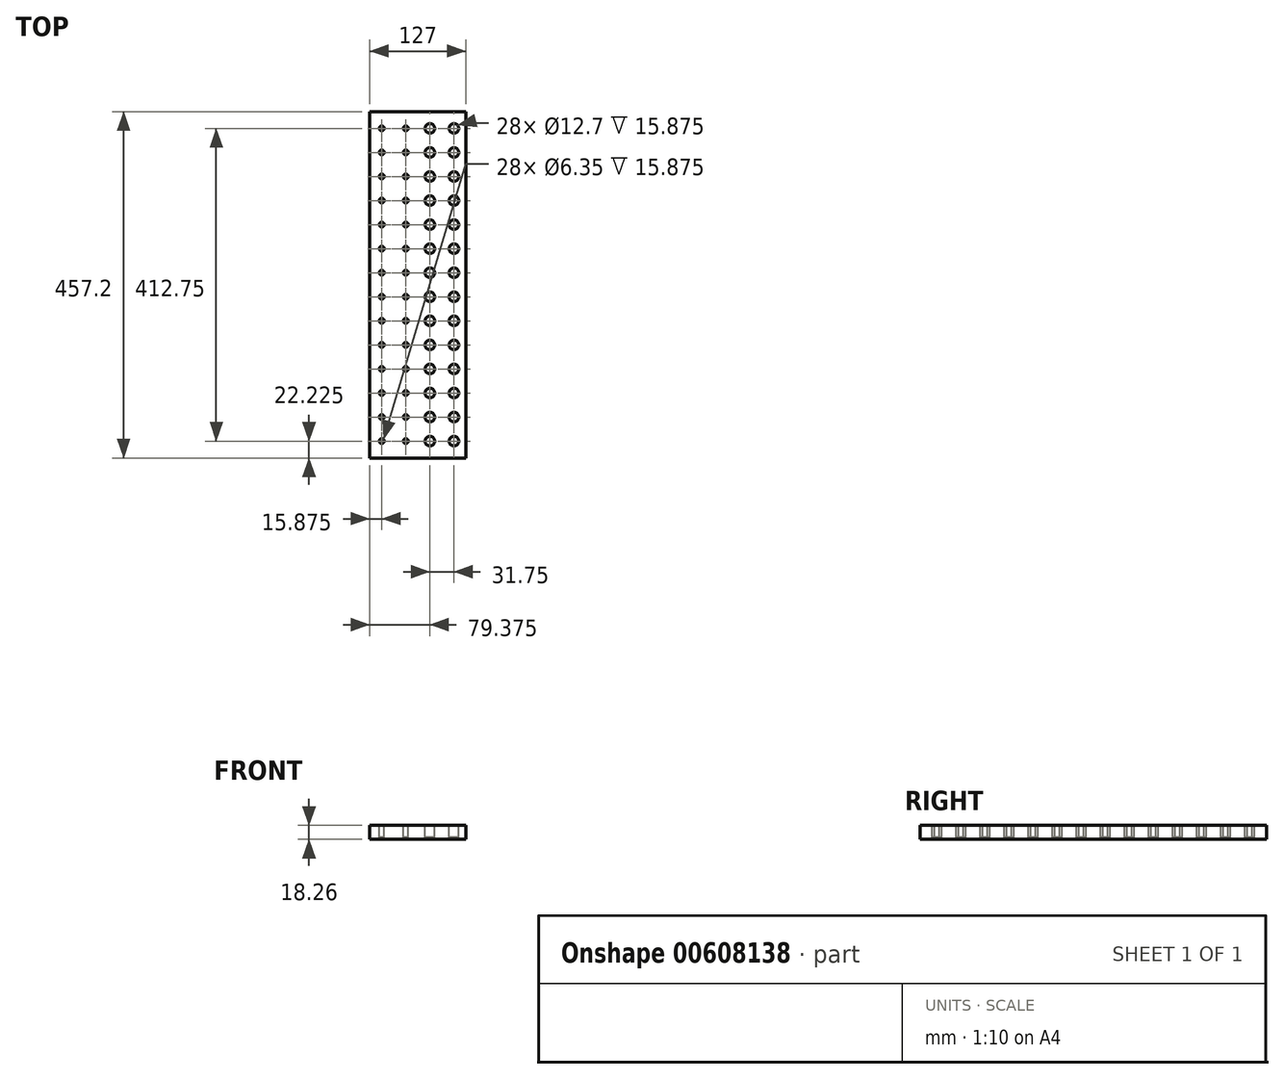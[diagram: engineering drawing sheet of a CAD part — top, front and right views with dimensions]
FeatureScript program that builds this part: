
annotation { "Feature Type Name" : "Feature", "Feature Type Description" : "" }
export const myFeature = defineFeature(function(context is Context, id is Id, definition is map)
    precondition{}
    {
        {
            var Q0;
            Q0=qCreatedBy(makeId("Top.planeOp"),FACE);
            var sketch = newSketch(context, id + "F0", { "sketchPlane" : qUnion([Q0])});
            skLineSegment(sketch, "E0.bottom", {"start": v(63.5, -228.6) * mm, "end": v(-63.5, -228.6) * mm});
            skLineSegment(sketch, "E0.top", {"start": v(63.5, 228.6) * mm, "end": v(-63.5, 228.6) * mm});
            skLineSegment(sketch, "E0.left", {"start": v(63.5, -228.6) * mm, "end": v(63.5, 228.6) * mm});
            skLineSegment(sketch, "E0.right", {"start": v(-63.5, -228.6) * mm, "end": v(-63.5, 228.6) * mm});
            skPoint(sketch, "E0.middle", {"position": v(0, 0) * mm});
            skSolve(sketch);
        }
        {
            var Q0;
            Q0 = qSketchRegion(id + "F0", true);
            extrude(context, id + "F1", {"entities" : qUnion([Q0]), "depth" : 18.26 * mm, "offsetDistance" : 25.4 * mm});
        }
        {
            var Q0;
            Q0=makeQuery(id+"F1.opExtrude","CAP_FACE",FACE,{"disambiguationData":[OSD([sQuery(id+"F0.wireOp",EDGE,"E0.bottom"),sQuery(id+"F0.wireOp",EDGE,"E0.top"),sQuery(id+"F0.wireOp",EDGE,"E0.left"),sQuery(id+"F0.wireOp",EDGE,"E0.right")])],"isStart":false});
            var sketch = newSketch(context, id + "F2", { "sketchPlane" : qUnion([Q0])});
            skCircle(sketch, "E1", {"center": v(-47.63, 206.38) * mm, "radius": 15.88 * mm, "construction": true});
            skCircle(sketch, "E2.0.1.0", {"center": v(-47.63, 174.63) * mm, "radius": 15.88 * mm, "construction": true});
            skCircle(sketch, "E2.0.2.0", {"center": v(-47.63, 142.88) * mm, "radius": 15.88 * mm, "construction": true});
            skCircle(sketch, "E2.0.3.0", {"center": v(-47.63, 111.13) * mm, "radius": 15.88 * mm, "construction": true});
            skCircle(sketch, "E2.0.4.0", {"center": v(-47.63, 79.38) * mm, "radius": 15.88 * mm, "construction": true});
            skCircle(sketch, "E2.0.5.0", {"center": v(-47.63, 47.63) * mm, "radius": 15.88 * mm, "construction": true});
            skCircle(sketch, "E2.0.6.0", {"center": v(-47.63, 15.88) * mm, "radius": 15.88 * mm, "construction": true});
            skCircle(sketch, "E2.0.7.0", {"center": v(-47.63, -15.87) * mm, "radius": 15.88 * mm, "construction": true});
            skCircle(sketch, "E2.0.8.0", {"center": v(-47.63, -47.62) * mm, "radius": 15.88 * mm, "construction": true});
            skCircle(sketch, "E2.0.9.0", {"center": v(-47.63, -79.37) * mm, "radius": 15.88 * mm, "construction": true});
            skCircle(sketch, "E2.0.10.0", {"center": v(-47.63, -111.12) * mm, "radius": 15.88 * mm, "construction": true});
            skCircle(sketch, "E2.0.11.0", {"center": v(-47.63, -142.87) * mm, "radius": 15.88 * mm, "construction": true});
            skCircle(sketch, "E2.0.12.0", {"center": v(-47.63, -174.62) * mm, "radius": 15.88 * mm, "construction": true});
            skCircle(sketch, "E2.0.13.0", {"center": v(-47.63, -206.37) * mm, "radius": 15.88 * mm, "construction": true});
            skCircle(sketch, "E2.1.0.0", {"center": v(-15.88, 206.38) * mm, "radius": 15.88 * mm, "construction": true});
            skCircle(sketch, "E2.1.1.0", {"center": v(-15.88, 174.63) * mm, "radius": 15.88 * mm, "construction": true});
            skCircle(sketch, "E2.1.2.0", {"center": v(-15.88, 142.88) * mm, "radius": 15.88 * mm, "construction": true});
            skCircle(sketch, "E2.1.3.0", {"center": v(-15.88, 111.13) * mm, "radius": 15.88 * mm, "construction": true});
            skCircle(sketch, "E2.1.4.0", {"center": v(-15.88, 79.38) * mm, "radius": 15.88 * mm, "construction": true});
            skCircle(sketch, "E2.1.5.0", {"center": v(-15.88, 47.63) * mm, "radius": 15.88 * mm, "construction": true});
            skCircle(sketch, "E2.1.6.0", {"center": v(-15.88, 15.88) * mm, "radius": 15.88 * mm, "construction": true});
            skCircle(sketch, "E2.1.7.0", {"center": v(-15.88, -15.87) * mm, "radius": 15.88 * mm, "construction": true});
            skCircle(sketch, "E2.1.8.0", {"center": v(-15.88, -47.62) * mm, "radius": 15.88 * mm, "construction": true});
            skCircle(sketch, "E2.1.9.0", {"center": v(-15.88, -79.37) * mm, "radius": 15.88 * mm, "construction": true});
            skCircle(sketch, "E2.1.10.0", {"center": v(-15.88, -111.12) * mm, "radius": 15.88 * mm, "construction": true});
            skCircle(sketch, "E2.1.11.0", {"center": v(-15.88, -142.87) * mm, "radius": 15.88 * mm, "construction": true});
            skCircle(sketch, "E2.1.12.0", {"center": v(-15.88, -174.62) * mm, "radius": 15.88 * mm, "construction": true});
            skCircle(sketch, "E2.1.13.0", {"center": v(-15.88, -206.37) * mm, "radius": 15.88 * mm, "construction": true});
            skCircle(sketch, "E2.2.0.0", {"center": v(15.87, 206.38) * mm, "radius": 15.88 * mm, "construction": true});
            skCircle(sketch, "E2.2.1.0", {"center": v(15.87, 174.63) * mm, "radius": 15.88 * mm, "construction": true});
            skCircle(sketch, "E2.2.2.0", {"center": v(15.87, 142.88) * mm, "radius": 15.88 * mm, "construction": true});
            skCircle(sketch, "E2.2.3.0", {"center": v(15.87, 111.13) * mm, "radius": 15.88 * mm, "construction": true});
            skCircle(sketch, "E2.2.4.0", {"center": v(15.87, 79.38) * mm, "radius": 15.88 * mm, "construction": true});
            skCircle(sketch, "E2.2.5.0", {"center": v(15.87, 47.63) * mm, "radius": 15.88 * mm, "construction": true});
            skCircle(sketch, "E2.2.6.0", {"center": v(15.87, 15.88) * mm, "radius": 15.88 * mm, "construction": true});
            skCircle(sketch, "E2.2.7.0", {"center": v(15.87, -15.87) * mm, "radius": 15.88 * mm, "construction": true});
            skCircle(sketch, "E2.2.8.0", {"center": v(15.87, -47.62) * mm, "radius": 15.88 * mm, "construction": true});
            skCircle(sketch, "E2.2.9.0", {"center": v(15.87, -79.37) * mm, "radius": 15.88 * mm, "construction": true});
            skCircle(sketch, "E2.2.10.0", {"center": v(15.87, -111.12) * mm, "radius": 15.88 * mm, "construction": true});
            skCircle(sketch, "E2.2.11.0", {"center": v(15.87, -142.87) * mm, "radius": 15.88 * mm, "construction": true});
            skCircle(sketch, "E2.2.12.0", {"center": v(15.87, -174.62) * mm, "radius": 15.88 * mm, "construction": true});
            skCircle(sketch, "E2.2.13.0", {"center": v(15.87, -206.37) * mm, "radius": 15.88 * mm, "construction": true});
            skCircle(sketch, "E2.3.0.0", {"center": v(47.62, 206.38) * mm, "radius": 15.88 * mm, "construction": true});
            skCircle(sketch, "E2.3.1.0", {"center": v(47.62, 174.63) * mm, "radius": 15.88 * mm, "construction": true});
            skCircle(sketch, "E2.3.2.0", {"center": v(47.62, 142.88) * mm, "radius": 15.88 * mm, "construction": true});
            skCircle(sketch, "E2.3.3.0", {"center": v(47.62, 111.13) * mm, "radius": 15.88 * mm, "construction": true});
            skCircle(sketch, "E2.3.4.0", {"center": v(47.62, 79.38) * mm, "radius": 15.88 * mm, "construction": true});
            skCircle(sketch, "E2.3.5.0", {"center": v(47.62, 47.63) * mm, "radius": 15.88 * mm, "construction": true});
            skCircle(sketch, "E2.3.6.0", {"center": v(47.62, 15.88) * mm, "radius": 15.88 * mm, "construction": true});
            skCircle(sketch, "E2.3.7.0", {"center": v(47.62, -15.87) * mm, "radius": 15.88 * mm, "construction": true});
            skCircle(sketch, "E2.3.8.0", {"center": v(47.62, -47.62) * mm, "radius": 15.88 * mm, "construction": true});
            skCircle(sketch, "E2.3.9.0", {"center": v(47.62, -79.37) * mm, "radius": 15.88 * mm, "construction": true});
            skCircle(sketch, "E2.3.10.0", {"center": v(47.62, -111.12) * mm, "radius": 15.88 * mm, "construction": true});
            skCircle(sketch, "E2.3.11.0", {"center": v(47.62, -142.87) * mm, "radius": 15.88 * mm, "construction": true});
            skCircle(sketch, "E2.3.12.0", {"center": v(47.62, -174.62) * mm, "radius": 15.88 * mm, "construction": true});
            skCircle(sketch, "E2.3.13.0", {"center": v(47.62, -206.37) * mm, "radius": 15.88 * mm, "construction": true});
            skLineSegment(sketch, "E2.direction1", {"start": v(-47.63, 206.38) * mm, "end": v(-15.88, 206.38) * mm, "construction": true});
            skLineSegment(sketch, "E2.direction2", {"start": v(-47.63, 206.38) * mm, "end": v(-47.63, 174.63) * mm, "construction": true});
            skCircle(sketch, "E3", {"center": v(47.62, 206.38) * mm, "radius": 6.35 * mm});
            skCircle(sketch, "E4", {"center": v(-47.63, 206.38) * mm, "radius": 3.18 * mm});
            skCircle(sketch, "E5.0.1.0", {"center": v(47.62, 174.63) * mm, "radius": 6.35 * mm});
            skCircle(sketch, "E5.0.2.0", {"center": v(47.62, 142.88) * mm, "radius": 6.35 * mm});
            skCircle(sketch, "E5.0.3.0", {"center": v(47.62, 111.13) * mm, "radius": 6.35 * mm});
            skCircle(sketch, "E5.0.4.0", {"center": v(47.62, 79.38) * mm, "radius": 6.35 * mm});
            skCircle(sketch, "E5.0.5.0", {"center": v(47.62, 47.63) * mm, "radius": 6.35 * mm});
            skCircle(sketch, "E5.0.6.0", {"center": v(47.62, 15.88) * mm, "radius": 6.35 * mm});
            skCircle(sketch, "E5.0.7.0", {"center": v(47.62, -15.87) * mm, "radius": 6.35 * mm});
            skCircle(sketch, "E5.0.8.0", {"center": v(47.62, -47.62) * mm, "radius": 6.35 * mm});
            skCircle(sketch, "E5.0.9.0", {"center": v(47.62, -79.37) * mm, "radius": 6.35 * mm});
            skCircle(sketch, "E5.0.10.0", {"center": v(47.62, -111.12) * mm, "radius": 6.35 * mm});
            skCircle(sketch, "E5.0.11.0", {"center": v(47.62, -142.87) * mm, "radius": 6.35 * mm});
            skCircle(sketch, "E5.0.12.0", {"center": v(47.62, -174.62) * mm, "radius": 6.35 * mm});
            skCircle(sketch, "E5.0.13.0", {"center": v(47.62, -206.37) * mm, "radius": 6.35 * mm});
            skCircle(sketch, "E5.1.0.0", {"center": v(15.87, 206.38) * mm, "radius": 6.35 * mm});
            skCircle(sketch, "E5.1.1.0", {"center": v(15.87, 174.63) * mm, "radius": 6.35 * mm});
            skCircle(sketch, "E5.1.2.0", {"center": v(15.87, 142.88) * mm, "radius": 6.35 * mm});
            skCircle(sketch, "E5.1.3.0", {"center": v(15.87, 111.13) * mm, "radius": 6.35 * mm});
            skCircle(sketch, "E5.1.4.0", {"center": v(15.87, 79.38) * mm, "radius": 6.35 * mm});
            skCircle(sketch, "E5.1.5.0", {"center": v(15.87, 47.63) * mm, "radius": 6.35 * mm});
            skCircle(sketch, "E5.1.6.0", {"center": v(15.87, 15.88) * mm, "radius": 6.35 * mm});
            skCircle(sketch, "E5.1.7.0", {"center": v(15.87, -15.87) * mm, "radius": 6.35 * mm});
            skCircle(sketch, "E5.1.8.0", {"center": v(15.87, -47.62) * mm, "radius": 6.35 * mm});
            skCircle(sketch, "E5.1.9.0", {"center": v(15.87, -79.37) * mm, "radius": 6.35 * mm});
            skCircle(sketch, "E5.1.10.0", {"center": v(15.87, -111.12) * mm, "radius": 6.35 * mm});
            skCircle(sketch, "E5.1.11.0", {"center": v(15.87, -142.87) * mm, "radius": 6.35 * mm});
            skCircle(sketch, "E5.1.12.0", {"center": v(15.87, -174.62) * mm, "radius": 6.35 * mm});
            skCircle(sketch, "E5.1.13.0", {"center": v(15.87, -206.37) * mm, "radius": 6.35 * mm});
            skLineSegment(sketch, "E5.direction1", {"start": v(47.62, 206.38) * mm, "end": v(15.87, 206.38) * mm, "construction": true});
            skLineSegment(sketch, "E5.direction2", {"start": v(47.62, 206.38) * mm, "end": v(47.62, 174.63) * mm, "construction": true});
            skCircle(sketch, "E6.0.1.0", {"center": v(-47.63, 174.63) * mm, "radius": 3.18 * mm});
            skCircle(sketch, "E6.0.2.0", {"center": v(-47.63, 142.88) * mm, "radius": 3.18 * mm});
            skCircle(sketch, "E6.0.3.0", {"center": v(-47.63, 111.13) * mm, "radius": 3.18 * mm});
            skCircle(sketch, "E6.0.4.0", {"center": v(-47.63, 79.38) * mm, "radius": 3.18 * mm});
            skCircle(sketch, "E6.0.5.0", {"center": v(-47.63, 47.63) * mm, "radius": 3.18 * mm});
            skCircle(sketch, "E6.0.6.0", {"center": v(-47.63, 15.88) * mm, "radius": 3.18 * mm});
            skCircle(sketch, "E6.0.7.0", {"center": v(-47.63, -15.87) * mm, "radius": 3.18 * mm});
            skCircle(sketch, "E6.0.8.0", {"center": v(-47.63, -47.62) * mm, "radius": 3.18 * mm});
            skCircle(sketch, "E6.0.9.0", {"center": v(-47.63, -79.37) * mm, "radius": 3.18 * mm});
            skCircle(sketch, "E6.0.10.0", {"center": v(-47.63, -111.12) * mm, "radius": 3.18 * mm});
            skCircle(sketch, "E6.0.11.0", {"center": v(-47.63, -142.87) * mm, "radius": 3.18 * mm});
            skCircle(sketch, "E6.0.12.0", {"center": v(-47.63, -174.62) * mm, "radius": 3.18 * mm});
            skCircle(sketch, "E6.0.13.0", {"center": v(-47.63, -206.37) * mm, "radius": 3.18 * mm});
            skCircle(sketch, "E6.1.0.0", {"center": v(-15.88, 206.38) * mm, "radius": 3.18 * mm});
            skCircle(sketch, "E6.1.1.0", {"center": v(-15.88, 174.63) * mm, "radius": 3.18 * mm});
            skCircle(sketch, "E6.1.2.0", {"center": v(-15.88, 142.88) * mm, "radius": 3.18 * mm});
            skCircle(sketch, "E6.1.3.0", {"center": v(-15.88, 111.13) * mm, "radius": 3.18 * mm});
            skCircle(sketch, "E6.1.4.0", {"center": v(-15.88, 79.38) * mm, "radius": 3.18 * mm});
            skCircle(sketch, "E6.1.5.0", {"center": v(-15.88, 47.63) * mm, "radius": 3.18 * mm});
            skCircle(sketch, "E6.1.6.0", {"center": v(-15.88, 15.88) * mm, "radius": 3.18 * mm});
            skCircle(sketch, "E6.1.7.0", {"center": v(-15.88, -15.87) * mm, "radius": 3.18 * mm});
            skCircle(sketch, "E6.1.8.0", {"center": v(-15.88, -47.62) * mm, "radius": 3.18 * mm});
            skCircle(sketch, "E6.1.9.0", {"center": v(-15.88, -79.37) * mm, "radius": 3.18 * mm});
            skCircle(sketch, "E6.1.10.0", {"center": v(-15.88, -111.12) * mm, "radius": 3.18 * mm});
            skCircle(sketch, "E6.1.11.0", {"center": v(-15.88, -142.87) * mm, "radius": 3.18 * mm});
            skCircle(sketch, "E6.1.12.0", {"center": v(-15.88, -174.62) * mm, "radius": 3.18 * mm});
            skCircle(sketch, "E6.1.13.0", {"center": v(-15.88, -206.37) * mm, "radius": 3.18 * mm});
            skSolve(sketch);
        }
        {
            var Q0;
            Q0 = qSketchRegion(id + "F2", true);
            extrude(context, id + "F3", {"entities" : qUnion([Q0]), "operationType" : NewBodyOperationType.REMOVE, "oppositeDirection" : true, "depth" : 15.88 * mm, "offsetDistance" : 25.4 * mm});
        }
    });
